# Revit family: P900013-031
name_source: partatom
category: Lighting Fixtures
revit_build: Autodesk Revit 2014 (Build: 20130308_1515(x64)
units: mm (PartAtom-declared; Revit-internal decimal feet)

## types (1)
- P900013-031
    Apparent Load = 60 VA
    Assembly Code = D5020200
    Color Filter = 16777215
    Connector Description = Lighting Connector
    Default Elevation = 48 "
    Description = Each lamp features an industrial styled-shade with an outer ribbed design and the capability to create different beam shapes as needed.
The directional frame is coated in a beautiful black finish.
Multi-directional lamp heads provide design flexibility and illuminate typically hard-to-reach areas
Ideal for any lobby, gallery, sitting room, hallway, or foyer.
Perfect for transitional or modern settings.
Measures 5-inch width by 5-15/16-inch height.
Uses one GU10 base bulb that is sold separately (50w max - LED or incandescent).
Able to be fully dimmable with dimmable bulbs.
Includes installation instructions and mounting hardware.
Progress Lighting products are designed for exceptional quality, reliability, and functionality.
    Dimming Lamp Color Temperature Shift = <None>
    Features = Manifest a swoon-worthy lighting experience with the stunning blend of modern and traditional styles in this one-of-a-kind semi-flush mount.
A beautiful black finish coats a handsome rectangular backplate.
Striking vintage light sockets boast their bold yet simple demeanors within the safety of sophisticated clear glass shades.
Ideal for any hallway, foyer, stairway, or kitchen.
Perfect for modern, new traditional, or contemporary settings.
Measures 13-inch width by 10-1/2-inch height.
Uses three medium base bulbs that are sold separately (60w max - LED or incandescent).
Able to be fully dimmable with dimmable bulbs.
Includes installation instructions and mounting hardware.
Progress Lighting products are designed for exceptional quality, reliability, and functionality.
    Fixture distribution = Direct
    Glass = Paint - Hubbell - White Texture
    Gold = Hubbell - Gold
    Height = 26.5 "
    Housing Material = Paint - Hubbell - Textured Camera Black
    Lamp = LED or Medium Base
    Load Classification = Lighting
    Manufacturer = Progress Lighting
    Model = P900013-031
    Photometric Web File = generic
    Power Factor = 1
    Product Documentation Link = https://hubbellcdn.com
    Product Link = https://www.hubbell.com
    Tilt Angle = 60.00°
    URL = https://www.hubbell.com
    Voltage = 120 V
    Warranty = 1 year Warranty
    Wattage Comments = 60W
    Watts = 60 W
    Width = 6 "

## geometry (parser evidence)
native form markers: Sweep x4
no freeform markers — native parametric forms only
